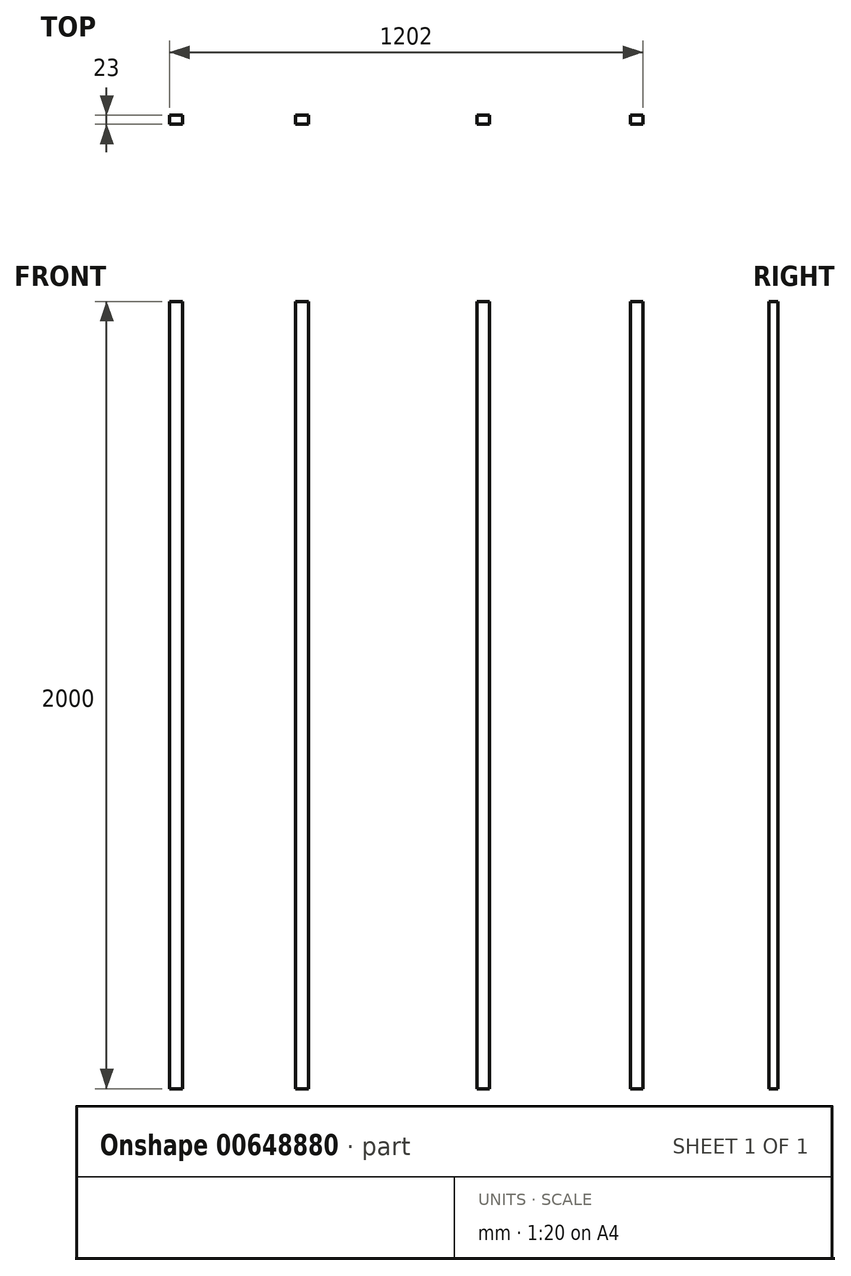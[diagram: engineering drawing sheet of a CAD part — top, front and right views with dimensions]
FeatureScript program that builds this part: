
annotation { "Feature Type Name" : "Feature", "Feature Type Description" : "" }
export const myFeature = defineFeature(function(context is Context, id is Id, definition is map)
    precondition{}
    {
        {
            var Q0;
            Q0=qCreatedBy(makeId("Top.planeOp"),FACE);
            var sketch = newSketch(context, id + "F0", { "sketchPlane" : qUnion([Q0])});
            skLineSegment(sketch, "E0.bottom", {"start": v(0, 0) * mm, "end": v(32, 0) * mm});
            skLineSegment(sketch, "E0.top", {"start": v(0, 23) * mm, "end": v(32, 23) * mm});
            skLineSegment(sketch, "E0.left", {"start": v(0, 0) * mm, "end": v(0, 23) * mm});
            skLineSegment(sketch, "E0.right", {"start": v(32, 0) * mm, "end": v(32, 23) * mm});
            skSolve(sketch);
        }
        {
            var Q0;
            Q0=makeQuery(id+"F0.imprint","IMPRINT",FACE,{"disambiguationData":[TD([[makeQuery(id+"F0.imprint","IMPRINT",EDGE,{"derivedFrom":sQuery(id+"F0.wireOp",EDGE,"E0.bottom")}),1.0]])]});
            extrude(context, id + "F1", {"entities" : qUnion([Q0]), "depth" : 2000 * mm, "offsetDistance" : 25 * mm});
        }
        {
            var Q0;
            Q0=makeQuery(id+"F1.opExtrude","SWEPT_BODY",BODY,{"disambiguationData":[OSD([sQuery(id+"F0.wireOp",EDGE,"E0.bottom"),sQuery(id+"F0.wireOp",EDGE,"E0.top"),sQuery(id+"F0.wireOp",EDGE,"E0.left"),sQuery(id+"F0.wireOp",EDGE,"E0.right")])]});
            transform(context, id + "F2", {"entities" : qUnion([Q0]), "transformType" : TransformType.TRANSLATION_3D, "dx" : 320 * mm, "dy" : 0 * mm, "dz" : 0 * mm, "makeCopy" : true});
        }
        {
            var Q0;
            Q0=makeQuery(id+"F2.opPattern","COPY",BODY,{"derivedFrom":makeQuery(id+"F1.opExtrude","SWEPT_BODY",BODY,{"disambiguationData":[OSD([sQuery(id+"F0.wireOp",EDGE,"E0.bottom"),sQuery(id+"F0.wireOp",EDGE,"E0.top"),sQuery(id+"F0.wireOp",EDGE,"E0.left"),sQuery(id+"F0.wireOp",EDGE,"E0.right")])]}),"instanceName":"1"});
            transform(context, id + "F3", {"entities" : qUnion([Q0]), "transformType" : TransformType.TRANSLATION_3D, "dx" : 460 * mm, "dy" : 0 * mm, "dz" : 0 * mm, "makeCopy" : true});
        }
        {
            var Q0;
            Q0=makeQuery(id+"F1.opExtrude","SWEPT_BODY",BODY,{"disambiguationData":[OSD([sQuery(id+"F0.wireOp",EDGE,"E0.bottom"),sQuery(id+"F0.wireOp",EDGE,"E0.top"),sQuery(id+"F0.wireOp",EDGE,"E0.left"),sQuery(id+"F0.wireOp",EDGE,"E0.right")])]});
            transform(context, id + "F4", {"entities" : qUnion([Q0]), "transformType" : TransformType.TRANSLATION_3D, "dx" : 1170 * mm, "dy" : 0 * mm, "dz" : 0 * mm, "makeCopy" : true});
        }
    });
